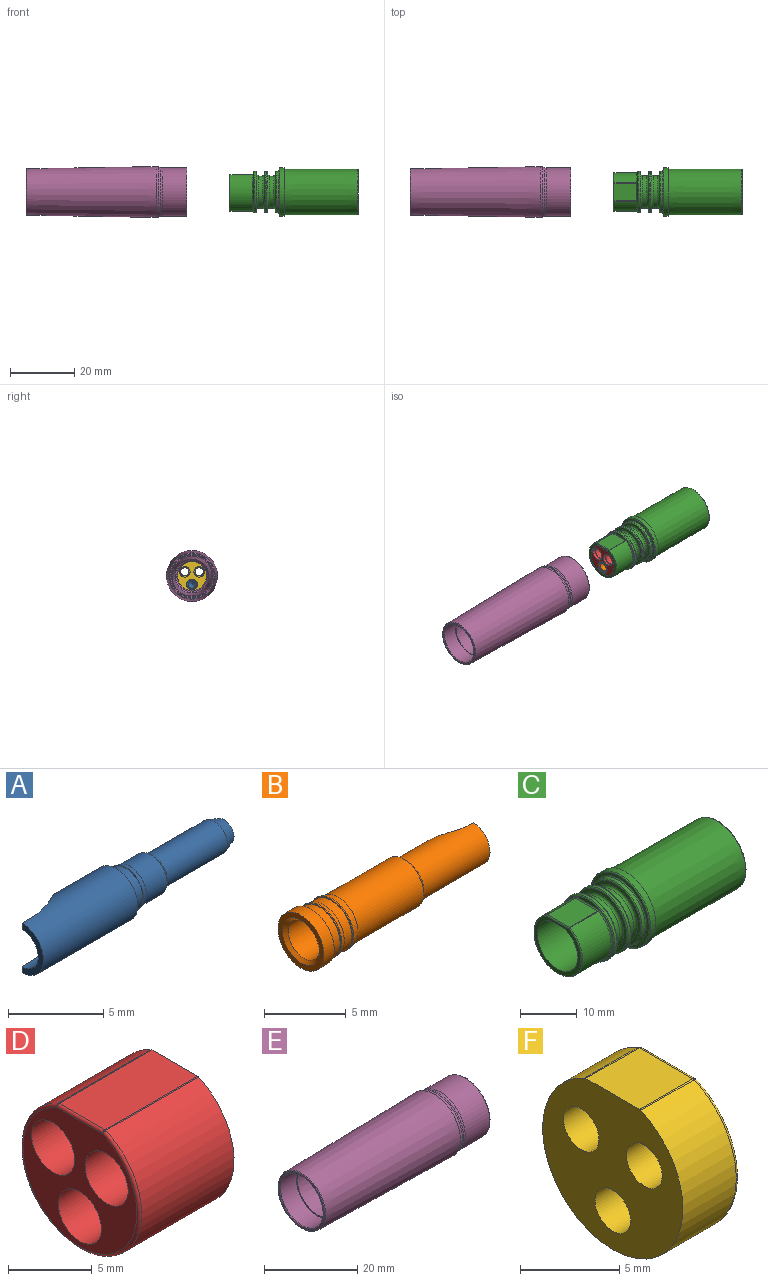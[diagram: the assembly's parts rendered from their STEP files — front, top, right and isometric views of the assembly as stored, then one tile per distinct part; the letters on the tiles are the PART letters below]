
ASSEMBLY  parts=6 mates=5
PART A: 16 faces, bbox 15x3.2x3.2 mm
  f0: cone r=1.19mm half-angle=59deg, axis (-1,0,0), area 5.2mm2, adj f7
  f1: cylinder r=1.26mm len=2.51mm, axis (-1,0,0), area 5.6mm2, adj f11,f12
  f2: cone r=1.22mm half-angle=15deg, axis (-1,0,0), area 2.5mm2, adj f3,f11
  f3: cylinder r=1.22mm len=2.44mm, axis (-1,0,0), area 11.6mm2, adj f2,f4
  f4: cone r=0.99mm half-angle=45deg, axis (-1,0,0), area 2.2mm2, adj f3,f5
  f5: cylinder r=0.99mm len=4.47mm, axis (-1,0,0), area 27.8mm2, adj f4,f6
  f6: cone r=0.71mm half-angle=20deg, axis (-1,0,0), area 4.3mm2, adj f5,f10
  f7: cylinder r=1.19mm len=5.72mm, axis (-1,0,0), area 23.8mm2, adj f0,f9,f13,f14,f15
  f8: cylinder r=1.59mm len=6.99mm, axis (-1,0,0), area 54mm2, adj f9,f12,f13,f14,f15
  f9: plane 3.18x1.59mm, normal (-1,0,0), area 1.7mm2, adj f7,f8,f13,f14
  f10: plane 1.43x1.43mm, normal (1,0,0), area 1.6mm2, adj f6
  f11: plane 2.6x2.6mm, normal (-1,0,0), area 0.4mm2, adj f1,f2
  f12: plane 3.18x3.18mm, normal (1,0,0), area 3mm2, adj f1,f8
  f13: plane 0.64x0.39mm, normal (0,1,0), area 0.3mm2, adj f7,f8,f9,f15
  f14: plane 0.64x0.39mm, normal (0,1,0), area 0.3mm2, adj f7,f8,f9,f15
  f15: cylinder r=3.96mm len=3.18mm, axis (0,0,-1), area 5.8mm2, adj f7,f8,f13,f14
PART B: 21 faces, bbox 14.9x4x4 mm
  f0: cone r=1.19mm half-angle=59deg, axis (1,0,0), area 5.2mm2, adj f13
  f1: cone r=1.6mm half-angle=45deg, axis (-1,0,0), area 3.2mm2, adj f2,f19
  f2: cylinder r=1.35mm len=6.74mm, axis (-1,0,0), area 57.3mm2, adj f1,f3
  f3: cone r=1.35mm half-angle=59deg, axis (-1,0,0), area 6.7mm2, adj f2
  f4: cone r=1.46mm half-angle=45deg, axis (-1,0,0), area 3.6mm2, adj f5,f14
  f5: cylinder r=1.71mm len=5.68mm, axis (-1,0,0), area 61.1mm2, adj f4,f6
  f6: cone r=1.71mm half-angle=15deg, axis (-1,0,0), area 6.1mm2, adj f5,f7
  f7: cylinder r=1.85mm len=3.71mm, axis (-1,0,0), area 0.9mm2, adj f6,f18
  f8: cylinder r=1.78mm len=3.56mm, axis (-1,0,0), area 7.3mm2, adj f9,f18
  f9: cone r=1.78mm half-angle=15deg, axis (-1,0,0), area 3.4mm2, adj f8,f10
  f10: cylinder r=1.85mm len=3.71mm, axis (-1,0,0), area 0.9mm2, adj f9,f17
  f11: cylinder r=1.78mm len=3.56mm, axis (-1,0,0), area 7.9mm2, adj f16,f17
  f12: cylinder r=1.98mm len=3.96mm, axis (-1,0,0), area 11.1mm2, adj f16,f19
  f13: cylinder r=1.19mm len=5.72mm, axis (1,0,0), area 34.2mm2, adj f0,f15,f20
  f14: cylinder r=1.46mm len=5.72mm, axis (-1,0,0), area 40.8mm2, adj f4,f15,f20
  f15: plane 2.92x1.46mm, normal (1,0,0), area 1.1mm2, adj f13,f14,f20
  f16: plane 3.96x3.96mm, normal (1,0,0), area 2.4mm2, adj f11,f12
  f17: plane 3.71x3.71mm, normal (-1,0,0), area 0.9mm2, adj f10,f11
  f18: plane 3.71x3.71mm, normal (-1,0,0), area 0.9mm2, adj f7,f8
  f19: plane 3.96x3.96mm, normal (-1,0,0), area 4.3mm2, adj f1,f12
  f20: cylinder r=3.96mm len=3.18mm, axis (0,0,-1), area 2.4mm2, adj f13,f14,f15
PART C: 59 faces, bbox 40x16.2x16.2 mm
  f0: cylinder r=5mm len=10mm, axis (1,0,0), area 213mm2, adj f1,f50,f54,f56
  f1: plane 11.6x10.9mm, normal (-1,0,0), area 25.6mm2, adj f0,f29,f30,f39,f50,f56
  f2: cylinder r=6mm len=12mm, axis (1,0,0), area 225.4mm2, adj f29,f41,f43,f46
  f3: plane 9.6x9.2mm, normal (-1,0,0), area 7.9mm2, adj f4,f49,f53,f54
  f4: cylinder r=4.5mm len=9mm, axis (1,0,0), area 181.3mm2, adj f3,f51,f57
  f5: cone r=5.53mm half-angle=45deg, axis (1,0,0), area 20.5mm2, adj f57,f58
  f6: cone r=6.2mm half-angle=2deg, axis (1,0,0), area 692.2mm2, adj f7,f58
  f7: plane 13x13mm, normal (1,0,0), area 12mm2, adj f6,f8
  f8: cylinder r=6.5mm len=13mm, axis (1,0,0), area 196mm2, adj f7,f31
  f9: plane 13.72x13.72mm, normal (1,0,0), area 6.8mm2, adj f31,f32
  f10: cone r=7.1mm half-angle=0.1deg, axis (-1,0,0), area 1014.3mm2, adj f11,f32
  f11: plane 15x15mm, normal (1,0,0), area 18.3mm2, adj f10,f12
  f12: cylinder r=7.5mm len=15mm, axis (1,0,0), area 61.3mm2, adj f11,f33
  f13: plane 14.6x14.6mm, normal (-1,0,0), area 26.4mm2, adj f33,f34
  f14: cylinder r=6.5mm len=13mm, axis (1,0,0), area 31.6mm2, adj f34,f35
  f15: plane 12.6x12.6mm, normal (-1,0,0), area 26.9mm2, adj f24,f35
  f16: cylinder r=5.08mm len=10.16mm, axis (1,0,0), area 45.1mm2, adj f24,f25
  f17: plane 12.6x12.6mm, normal (1,0,0), area 26.9mm2, adj f25,f36
  f18: cylinder r=6.5mm len=13mm, axis (1,0,0), area 24.5mm2, adj f36,f37
  f19: plane 12.6x12.6mm, normal (-1,0,0), area 26.9mm2, adj f26,f37
  f20: cylinder r=5.08mm len=10.16mm, axis (1,0,0), area 45.1mm2, adj f26,f27
  f21: plane 12.6x12.6mm, normal (1,0,0), area 26.9mm2, adj f27,f38
  f22: cylinder r=6.5mm len=13mm, axis (1,0,0), area 24.5mm2, adj f38,f48
  f23: plane 12.6x12.6mm, normal (-1,0,0), area 6.6mm2, adj f42,f43,f44,f45,f48
  f24: torus R=5.58mm, axis (1,0,0), area 26mm2, adj f15,f16
  f25: torus R=5.58mm, axis (-1,0,0), area 26mm2, adj f16,f17
  f26: torus R=5.58mm, axis (1,0,0), area 26mm2, adj f19,f20
  f27: torus R=5.58mm, axis (-1,0,0), area 26mm2, adj f20,f21
  f28: plane 7.1x5.52mm, normal (0,0,1), area 39.2mm2, adj f30,f41,f44,f46
  f29: torus R=5.8mm, axis (1,0,0), area 9.9mm2, adj f1,f2,f40,f47
  f30: cylinder r=0.2mm len=5.52mm, axis (0,-1,0), area 1.7mm2, adj f1,f28,f40,f47
  f31: torus R=6.7mm, axis (-1,0,0), area 13mm2, adj f8,f9
  f32: torus R=6.86mm, axis (-1,0,0), area 13.8mm2, adj f9,f10
  f33: torus R=7.3mm, axis (1,0,0), area 14.7mm2, adj f12,f13
  f34: torus R=6.7mm, axis (1,0,0), area 13mm2, adj f13,f14
  f35: torus R=6.3mm, axis (1,0,0), area 12.7mm2, adj f14,f15
  f36: torus R=6.3mm, axis (-1,0,0), area 12.7mm2, adj f17,f18
  f37: torus R=6.3mm, axis (1,0,0), area 12.7mm2, adj f18,f19
  f38: torus R=6.3mm, axis (-1,0,0), area 12.7mm2, adj f21,f22
  f39: plane 7.83x3.84mm, normal (0,0,-1), area 30mm2, adj f1,f49,f50,f51,f53,f56
  f40: sphere r=0.2mm, area 0mm2, adj f29,f30,f41
  f41: cylinder r=0.2mm len=7.1mm, axis (1,0,0), area 0.7mm2, adj f2,f28,f40,f42
  f42: torus R=0.4mm, axis (1,0,0), area 0mm2, adj f23,f41,f43,f44
  f43: torus R=6.2mm, axis (1,0,0), area 10.1mm2, adj f2,f23,f42,f45
  f44: cylinder r=0.2mm len=5.52mm, axis (0,1,0), area 1.7mm2, adj f23,f28,f42,f45
  f45: torus R=0.4mm, axis (1,0,0), area 0mm2, adj f23,f43,f44,f46
  f46: cylinder r=0.2mm len=7.1mm, axis (1,0,0), area 0.7mm2, adj f2,f28,f45,f47
  f47: sphere r=0.2mm, area 0mm2, adj f29,f30,f46
  f48: torus R=6.3mm, axis (1,0,0), area 12.7mm2, adj f22,f23
  f49: cylinder r=0.2mm len=0.98mm, axis (0,-1,0), area 0.3mm2, adj f3,f39,f51,f52
  f50: cylinder r=0.2mm len=7.8mm, axis (1,0,0), area 0.6mm2, adj f0,f1,f39,f52
  f51: bspline ~1.89x0.2mm, area 0.5mm2, adj f4,f39,f49,f53
  f52: sphere r=0.2mm, area 0mm2, adj f49,f50,f54
  f53: cylinder r=0.2mm len=0.98mm, axis (0,-1,0), area 0.3mm2, adj f3,f39,f51,f55
  f54: torus R=4.8mm, axis (-1,0,0), area 8.5mm2, adj f0,f3,f52,f55
  f55: sphere r=0.2mm, area 0mm2, adj f53,f54,f56
  f56: cylinder r=0.2mm len=7.8mm, axis (1,0,0), area 0.6mm2, adj f0,f1,f39,f55
  f57: torus R=5.5mm, axis (-1,0,0), area 22.7mm2, adj f4,f5
  f58: torus R=4.55mm, axis (1,0,0), area 25.7mm2, adj f5,f6
PART D: 19 faces, bbox 8x10.8x10.4 mm
  f0: plane 7.8x3.84mm, normal (0,0,1), area 29.9mm2, adj f2,f13,f16,f18
  f1: cylinder r=5mm len=10mm, axis (-1,0,0), area 213mm2, adj f2,f13,f15,f18
  f2: plane 10x9.6mm, normal (1,0,0), area 39.8mm2, adj f0,f1,f4,f6,f8,f13,f18
  f3: plane 9.6x9.2mm, normal (-1,0,0), area 40.3mm2, adj f10,f11,f12,f15,f16
  f4: cylinder r=2mm len=4mm, axis (1,0,0), area 11.3mm2, adj f2,f5
  f5: plane 4x4mm, normal (1,0,0), area 2.2mm2, adj f4,f12
  f6: cylinder r=2mm len=4mm, axis (1,0,0), area 11.3mm2, adj f2,f7
  f7: plane 4x4mm, normal (1,0,0), area 2.2mm2, adj f6,f11
  f8: cylinder r=2mm len=4mm, axis (1,0,0), area 11.3mm2, adj f2,f9
  f9: plane 4x4mm, normal (1,0,0), area 2.2mm2, adj f8,f10
  f10: cylinder r=1.81mm len=7.1mm, axis (1,0,0), area 81mm2, adj f3,f9
  f11: cylinder r=1.81mm len=7.1mm, axis (1,0,0), area 81mm2, adj f3,f7
  f12: cylinder r=1.81mm len=7.1mm, axis (1,0,0), area 81mm2, adj f3,f5
  f13: cylinder r=0.2mm len=7.8mm, axis (-1,0,0), area 0.6mm2, adj f0,f1,f2,f14
  f14: sphere r=0.2mm, area 0mm2, adj f13,f15,f16
  f15: torus R=4.8mm, axis (1,0,0), area 8.5mm2, adj f1,f3,f14,f17
  f16: cylinder r=0.2mm len=3.84mm, axis (0,-1,0), area 1.2mm2, adj f0,f3,f14,f17
  f17: sphere r=0.2mm, area 0mm2, adj f15,f16,f18
  f18: cylinder r=0.2mm len=7.8mm, axis (-1,0,0), area 0.6mm2, adj f0,f1,f2,f17
PART E: 45 faces, bbox 50x17.5x17.5 mm
  f0: plane 9.6x9.2mm, normal (1,0,0), area 7.9mm2, adj f13,f35,f39,f40
  f1: cylinder r=5mm len=10mm, axis (1,0,0), area 103.8mm2, adj f14,f36,f40,f42
  f2: cylinder r=6.1mm len=12.2mm, axis (1,0,0), area 229.5mm2, adj f24,f28,f29,f33
  f3: cylinder r=6.6mm len=13.2mm, axis (1,0,0), area 315.2mm2, adj f18,f34
  f4: plane 14.6x14.6mm, normal (1,0,0), area 22.1mm2, adj f18,f19
  f5: cylinder r=7.5mm len=15mm, axis (1,0,0), area 351.8mm2, adj f19,f22
  f6: cone r=7.5mm half-angle=19deg, axis (-1,0,0), area 28mm2, adj f22,f23
  f7: cone r=7.91mm half-angle=1deg, axis (1,0,0), area 1910.9mm2, adj f20,f23
  f8: cone r=7.2mm half-angle=89deg, axis (-1,0,0), area 13.1mm2, adj f20,f21
  f9: cylinder r=6.5mm len=13mm, axis (1,0,0), area 196.2mm2, adj f10,f21
  f10: plane 13x13mm, normal (-1,0,0), area 12mm2, adj f9,f11
  f11: cone r=5.38mm half-angle=2deg, axis (-1,0,0), area 845.9mm2, adj f10,f43
  f12: cone r=4.5mm half-angle=45deg, axis (-1,0,0), area 13.4mm2, adj f43,f44
  f13: cylinder r=4.5mm len=9mm, axis (1,0,0), area 16.6mm2, adj f0,f37,f44
  f14: plane 11.8x11.1mm, normal (1,0,0), area 29.2mm2, adj f1,f17,f24,f25,f36,f42
  f15: plane 12.8x12.8mm, normal (1,0,0), area 6.7mm2, adj f30,f31,f32,f33,f34
  f16: plane 7.1x5.58mm, normal (0,0,-1), area 39.6mm2, adj f25,f28,f29,f30
  f17: plane 3.84x3.83mm, normal (0,0,-1), area 14.6mm2, adj f14,f35,f36,f37,f39,f42
  f18: torus R=6.8mm, axis (1,0,0), area 13.2mm2, adj f3,f4
  f19: torus R=7.3mm, axis (1,0,0), area 14.7mm2, adj f4,f5
  f20: torus R=7mm, axis (-1,0,0), area 14.1mm2, adj f7,f8
  f21: torus R=6.7mm, axis (-1,0,0), area 12.8mm2, adj f8,f9
  f22: torus R=9.5mm, axis (1,0,0), area 31.4mm2, adj f5,f6
  f23: torus R=5.91mm, axis (-1,0,0), area 34.5mm2, adj f6,f7
  f24: torus R=5.9mm, axis (-1,0,0), area 10mm2, adj f2,f14,f26,f27
  f25: cylinder r=0.2mm len=5.58mm, axis (0,-1,0), area 1.8mm2, adj f14,f16,f26,f27
  f26: sphere r=0.2mm, area 0mm2, adj f24,f25,f28
  f27: sphere r=0.2mm, area 0mm2, adj f24,f25,f29
  f28: cylinder r=0.2mm len=7.1mm, axis (1,0,0), area 0.7mm2, adj f2,f16,f26,f31
  f29: cylinder r=0.2mm len=7.1mm, axis (1,0,0), area 0.7mm2, adj f2,f16,f27,f32
  f30: cylinder r=0.2mm len=5.58mm, axis (0,-1,0), area 1.8mm2, adj f15,f16,f31,f32
  f31: torus R=0.4mm, axis (-1,0,0), area 0mm2, adj f15,f28,f30,f33
  f32: torus R=0.4mm, axis (-1,0,0), area 0mm2, adj f15,f29,f30,f33
  f33: torus R=6.3mm, axis (-1,0,0), area 10.3mm2, adj f2,f15,f31,f32
  f34: torus R=6.4mm, axis (-1,0,0), area 12.9mm2, adj f3,f15
  f35: cylinder r=0.2mm len=0.98mm, axis (0,1,0), area 0.3mm2, adj f0,f17,f37,f38
  f36: cylinder r=0.2mm len=3.8mm, axis (1,0,0), area 0.3mm2, adj f1,f14,f17,f38
  f37: bspline ~1.89x0.2mm, area 0.5mm2, adj f13,f17,f35,f39
  f38: sphere r=0.2mm, area 0mm2, adj f35,f36,f40
  f39: cylinder r=0.2mm len=0.98mm, axis (0,1,0), area 0.3mm2, adj f0,f17,f37,f41
  f40: torus R=4.8mm, axis (1,0,0), area 8.5mm2, adj f0,f1,f38,f41
  f41: sphere r=0.2mm, area 0mm2, adj f39,f40,f42
  f42: cylinder r=0.2mm len=3.8mm, axis (1,0,0), area 0.3mm2, adj f1,f14,f17,f41
  f43: torus R=4.39mm, axis (1,0,0), area 24.9mm2, adj f11,f12
  f44: torus R=5.5mm, axis (-1,0,0), area 22.7mm2, adj f12,f13
PART F: 19 faces, bbox 4x10.8x10.4 mm
  f0: plane 3.84x3.8mm, normal (0,0,1), area 14.6mm2, adj f3,f13,f15,f18
  f1: cylinder r=5mm len=10mm, axis (-1,0,0), area 103.8mm2, adj f3,f13,f16,f18
  f2: plane 9.6x9.2mm, normal (1,0,0), area 45.7mm2, adj f4,f6,f8,f15,f16
  f3: plane 10x9.6mm, normal (-1,0,0), area 62.3mm2, adj f0,f1,f10,f11,f12,f13,f18
  f4: cylinder r=1.65mm len=3.3mm, axis (1,0,0), area 15.1mm2, adj f2,f5
  f5: plane 3.3x3.3mm, normal (1,0,0), area 3.5mm2, adj f4,f12
  f6: cylinder r=1.65mm len=3.3mm, axis (1,0,0), area 15.1mm2, adj f2,f7
  f7: plane 3.3x3.3mm, normal (1,0,0), area 3.5mm2, adj f6,f11
  f8: cylinder r=1.65mm len=3.3mm, axis (1,0,0), area 15.1mm2, adj f2,f9
  f9: plane 3.3x3.3mm, normal (1,0,0), area 3.5mm2, adj f8,f10
  f10: cylinder r=1.27mm len=2.54mm, axis (1,0,0), area 20.3mm2, adj f3,f9
  f11: cylinder r=1.27mm len=2.54mm, axis (1,0,0), area 20.3mm2, adj f3,f7
  f12: cylinder r=1.27mm len=2.54mm, axis (1,0,0), area 20.3mm2, adj f3,f5
  f13: cylinder r=0.2mm len=3.8mm, axis (-1,0,0), area 0.3mm2, adj f0,f1,f3,f14
  f14: sphere r=0.2mm, area 0mm2, adj f13,f15,f16
  f15: cylinder r=0.2mm len=3.84mm, axis (0,1,0), area 1.2mm2, adj f0,f2,f14,f17
  f16: torus R=4.8mm, axis (1,0,0), area 8.5mm2, adj f1,f2,f14,f17
  f17: sphere r=0.2mm, area 0mm2, adj f15,f16,f18
  f18: cylinder r=0.2mm len=3.8mm, axis (-1,0,0), area 0.3mm2, adj f0,f1,f3,f17
PLACE A rot(axis=(-1,0,0),135deg) t=(7.82,5.58,-0.58)mm
PLACE B rot(axis=(-1,0,0),118deg) t=(46.05,5.58,-0.58)mm
PLACE C t=(46.04,5.58,2.02)mm
PLACE D rot(axis=(0,0,1),180deg) t=(50.04,5.58,2.02)mm
PLACE E t=(32.84,5.58,2.02)mm fixed
PLACE F rot(axis=(0,0,1),180deg) t=(15.34,5.58,2.02)mm
MATE fastened D.f1 <-> C.f0  axis (-1,0,0) through (46.04,5.58,2.02)mm
MATE revolute F.f1 <-> E.f1  axis (1,0,0) through (15.44,5.58,2.02)mm
MATE revolute F.f8 <-> A.f0  axis (-1,0,0) through (14.8,5.58,-0.58)mm
MATE slider E.f1 <-> C.f0  axis (1,0,0) through (21.09,5.58,2.02)mm
MATE revolute B.f0 <-> D.f6  axis (1,0,0) through (46.94,5.58,-0.58)mm
